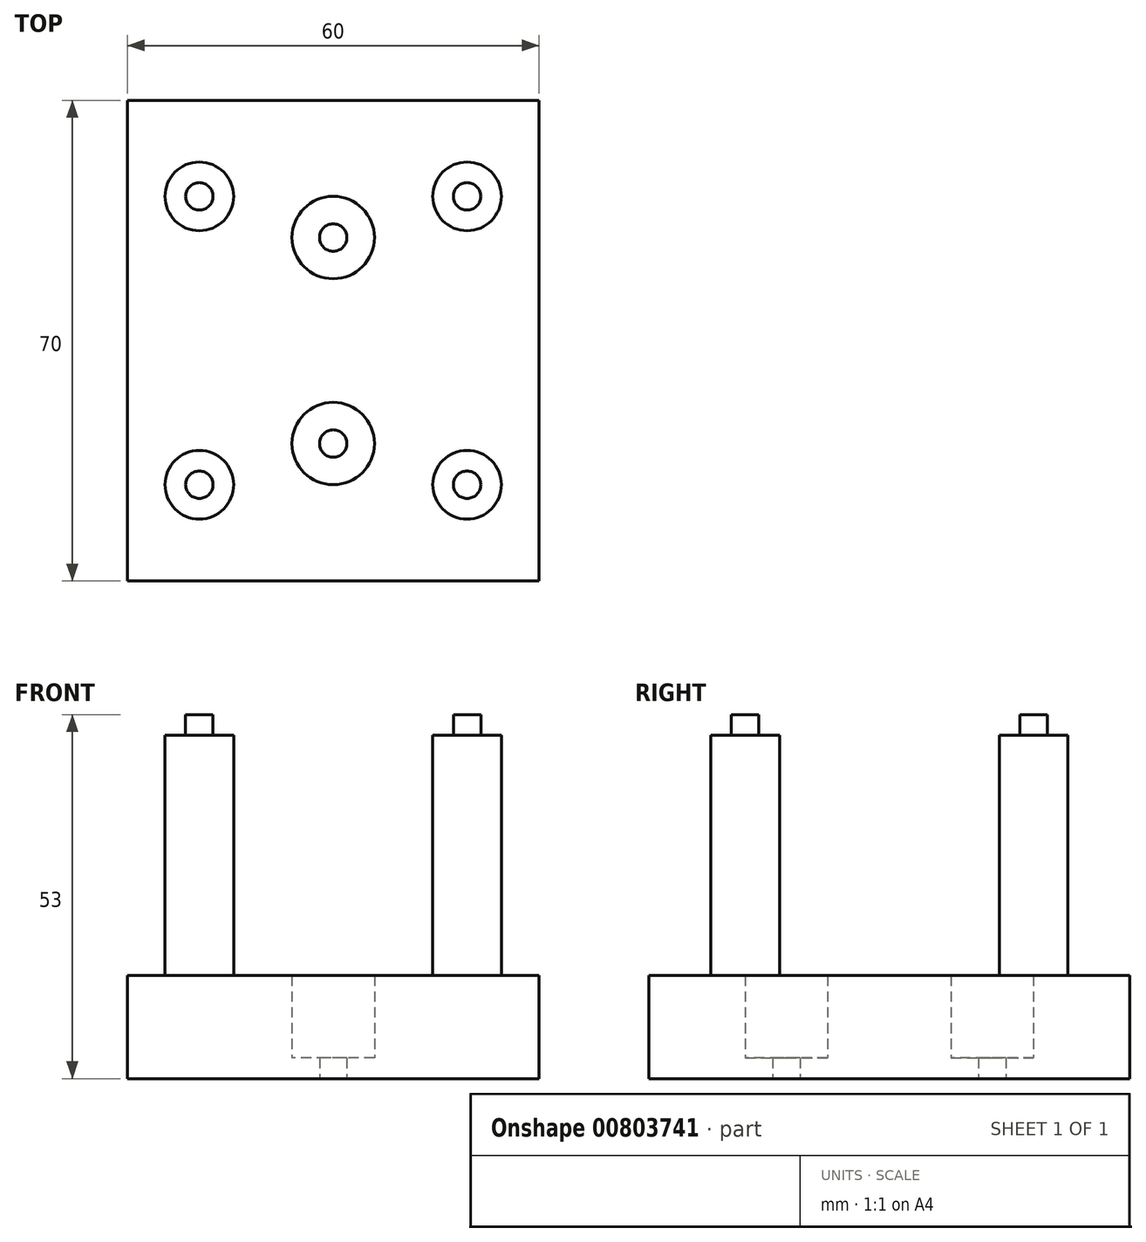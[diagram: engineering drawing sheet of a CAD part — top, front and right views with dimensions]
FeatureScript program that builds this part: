
annotation { "Feature Type Name" : "Feature", "Feature Type Description" : "" }
export const myFeature = defineFeature(function(context is Context, id is Id, definition is map)
    precondition{}
    {
        {
            var Q0;
            Q0=qCreatedBy(makeId("Top.planeOp"),FACE);
            var sketch = newSketch(context, id + "F0", { "sketchPlane" : qUnion([Q0])});
            skLineSegment(sketch, "E0.bottom", {"start": v(30, 35) * mm, "end": v(-30, 35) * mm});
            skLineSegment(sketch, "E0.top", {"start": v(30, -35) * mm, "end": v(-30, -35) * mm});
            skLineSegment(sketch, "E0.left", {"start": v(30, 35) * mm, "end": v(30, -35) * mm});
            skLineSegment(sketch, "E0.right", {"start": v(-30, 35) * mm, "end": v(-30, -35) * mm});
            skPoint(sketch, "E0.middle", {"position": v(0, 0) * mm});
            skCircle(sketch, "E1", {"center": v(19.5, 21) * mm, "radius": 2 * mm});
            skCircle(sketch, "E2", {"center": v(19.5, -21) * mm, "radius": 2 * mm});
            skCircle(sketch, "E3", {"center": v(-19.5, -21) * mm, "radius": 2 * mm});
            skCircle(sketch, "E4", {"center": v(-19.5, 21) * mm, "radius": 2 * mm});
            skCircle(sketch, "E5", {"center": v(-19.5, 21) * mm, "radius": 5 * mm});
            skCircle(sketch, "E6", {"center": v(19.5, 21) * mm, "radius": 5 * mm});
            skCircle(sketch, "E7", {"center": v(-19.5, -21) * mm, "radius": 5 * mm});
            skCircle(sketch, "E8", {"center": v(19.5, -21) * mm, "radius": 5 * mm});
            skLineSegment(sketch, "E9", {"start": v(0, 0) * mm, "end": v(0, 15) * mm});
            skCircle(sketch, "E10", {"center": v(0, 15) * mm, "radius": 6 * mm});
            skCircle(sketch, "E11", {"center": v(0, 15) * mm, "radius": 2 * mm});
            skLineSegment(sketch, "E12", {"start": v(0, 0) * mm, "end": v(0, -15) * mm});
            skCircle(sketch, "E13", {"center": v(0, -15) * mm, "radius": 6 * mm});
            skCircle(sketch, "E14", {"center": v(0, -15) * mm, "radius": 2 * mm});
            skLineSegment(sketch, "E15.bottom", {"start": v(-19.5, 21) * mm, "end": v(19.5, 21) * mm});
            skLineSegment(sketch, "E15.top", {"start": v(-19.5, -21) * mm, "end": v(19.5, -21) * mm});
            skLineSegment(sketch, "E15.left", {"start": v(-19.5, 21) * mm, "end": v(-19.5, -21) * mm});
            skLineSegment(sketch, "E15.right", {"start": v(19.5, 21) * mm, "end": v(19.5, -21) * mm});
            skLineSegment(sketch, "E16", {"start": v(0, 0) * mm, "end": v(19.5, 0) * mm});
            skSolve(sketch);
        }
        {
            var Q0;
            Q0 = qSketchRegion(id + "F0", true);
            var Q1;
            {var subQ5=sQuery(id+"F0.wireOp",EDGE,"E16");Q1=makeQuery(id+"F0.imprint","IMPRINT",FACE,{"disambiguationData":[TD([[makeQuery(id+"F0.imprint","IMPRINT",EDGE,{"derivedFrom":subQ5}),1.0]])]});}
            var Q2;
            {var subQ6=sQuery(id+"F0.wireOp",EDGE,"E5");var subQ10=sQuery(id+"F0.wireOp",EDGE,"E15.bottom");var subQ14=makeQuery(id+"F0.imprint","INTERSECT",VERTEX,{"derivedFrom":[subQ6,subQ10]});Q2=makeQuery(id+"F0.imprint","IMPRINT",FACE,{"disambiguationData":[TD([[makeQuery(id+"F0.imprint","IMPRINT",EDGE,{"disambiguationData":[TD([[subQ14,1.0]])],"derivedFrom":subQ6}),-1.0]])]});}
            var Q3;
            {var subQ7=sQuery(id+"F0.wireOp",EDGE,"E16");Q3=makeQuery(id+"F0.imprint","IMPRINT",FACE,{"disambiguationData":[TD([[makeQuery(id+"F0.imprint","IMPRINT",EDGE,{"derivedFrom":subQ7}),-1.0]])]});}
            extrude(context, id + "F1", {"entities" : qUnion([Q0, Q1, Q2, Q3]), "depth" : 15 * mm, "offsetDistance" : 25 * mm});
        }
        {
            var Q0;
            Q0=makeQuery(id+"F0.imprint","IMPRINT",FACE,{"disambiguationData":[TD([[makeQuery(id+"F0.imprint","IMPRINT",EDGE,{"derivedFrom":sQuery(id+"F0.wireOp",EDGE,"E1")}),-1.0]])]});
            var Q1;
            Q1=makeQuery(id+"F0.imprint","IMPRINT",FACE,{"disambiguationData":[TD([[makeQuery(id+"F0.imprint","IMPRINT",EDGE,{"derivedFrom":sQuery(id+"F0.wireOp",EDGE,"E4")}),-1.0]])]});
            var Q2;
            Q2=makeQuery(id+"F0.imprint","IMPRINT",FACE,{"disambiguationData":[TD([[makeQuery(id+"F0.imprint","IMPRINT",EDGE,{"derivedFrom":sQuery(id+"F0.wireOp",EDGE,"E3")}),-1.0]])]});
            var Q3;
            Q3=makeQuery(id+"F0.imprint","IMPRINT",FACE,{"disambiguationData":[TD([[makeQuery(id+"F0.imprint","IMPRINT",EDGE,{"derivedFrom":sQuery(id+"F0.wireOp",EDGE,"E2")}),-1.0]])]});
            extrude(context, id + "F2", {"entities" : qUnion([Q0, Q1, Q2, Q3]), "operationType" : NewBodyOperationType.ADD, "depth" : 50 * mm, "offsetDistance" : 25 * mm});
        }
        {
            var Q0;
            Q0=makeQuery(id+"F0.imprint","IMPRINT",FACE,{"disambiguationData":[TD([[makeQuery(id+"F0.imprint","IMPRINT",EDGE,{"derivedFrom":sQuery(id+"F0.wireOp",EDGE,"E3")}),1.0]])]});
            var Q1;
            Q1=makeQuery(id+"F0.imprint","IMPRINT",FACE,{"disambiguationData":[TD([[makeQuery(id+"F0.imprint","IMPRINT",EDGE,{"derivedFrom":sQuery(id+"F0.wireOp",EDGE,"E4")}),1.0]])]});
            var Q2;
            Q2=makeQuery(id+"F0.imprint","IMPRINT",FACE,{"disambiguationData":[TD([[makeQuery(id+"F0.imprint","IMPRINT",EDGE,{"derivedFrom":sQuery(id+"F0.wireOp",EDGE,"E2")}),1.0]])]});
            var Q3;
            Q3=makeQuery(id+"F0.imprint","IMPRINT",FACE,{"disambiguationData":[TD([[makeQuery(id+"F0.imprint","IMPRINT",EDGE,{"derivedFrom":sQuery(id+"F0.wireOp",EDGE,"E1")}),1.0]])]});
            extrude(context, id + "F3", {"entities" : qUnion([Q0, Q1, Q2, Q3]), "operationType" : NewBodyOperationType.ADD, "depth" : 53 * mm, "offsetDistance" : 25 * mm});
        }
        {
            var Q0;
            Q0=makeQuery(id+"F0.imprint","IMPRINT",FACE,{"disambiguationData":[TD([[makeQuery(id+"F0.imprint","IMPRINT",EDGE,{"derivedFrom":sQuery(id+"F0.wireOp",EDGE,"E11")}),-1.0]])]});
            var Q1;
            Q1=makeQuery(id+"F0.imprint","IMPRINT",FACE,{"disambiguationData":[TD([[makeQuery(id+"F0.imprint","IMPRINT",EDGE,{"derivedFrom":sQuery(id+"F0.wireOp",EDGE,"E14")}),-1.0]])]});
            extrude(context, id + "F4", {"entities" : qUnion([Q0, Q1]), "operationType" : NewBodyOperationType.ADD, "depth" : 3 * mm, "offsetDistance" : 25 * mm});
        }
    });
